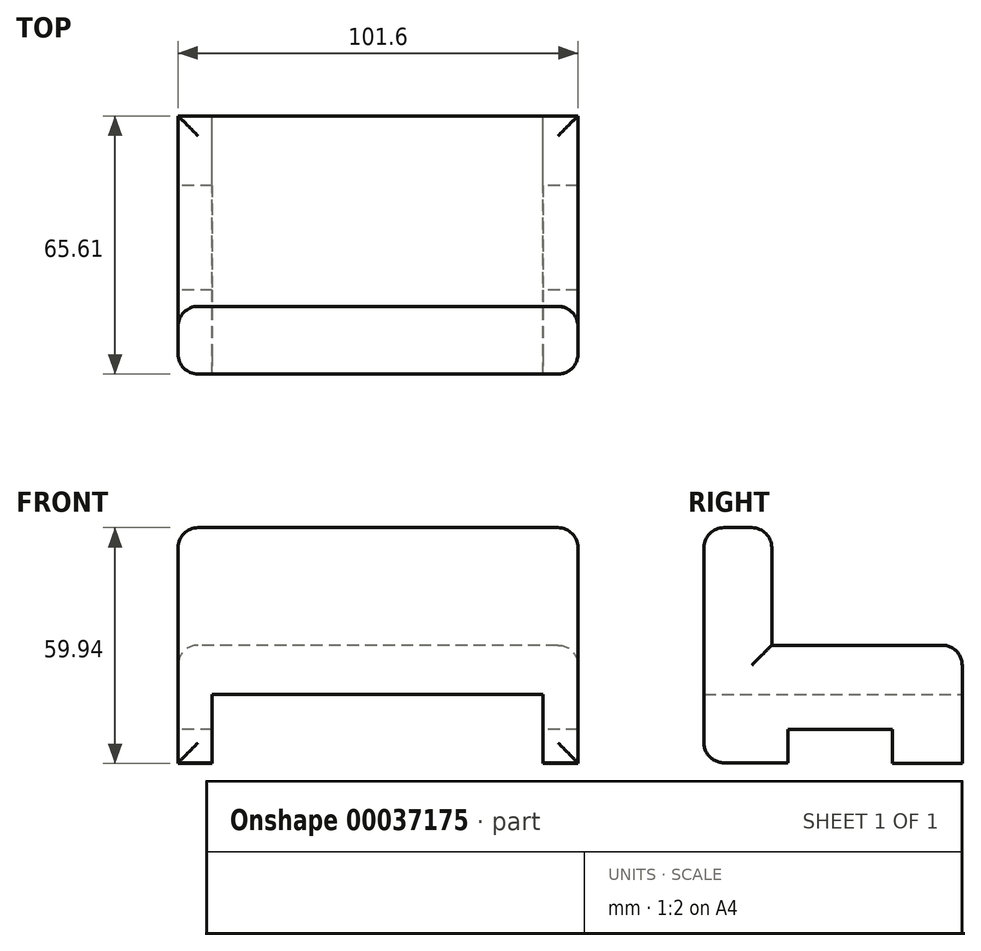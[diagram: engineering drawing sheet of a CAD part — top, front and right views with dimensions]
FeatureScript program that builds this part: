
annotation { "Feature Type Name" : "Feature", "Feature Type Description" : "" }
export const myFeature = defineFeature(function(context is Context, id is Id, definition is map)
    precondition{}
    {
        {
            var Q0;
            Q0=qCreatedBy(makeId("Right.planeOp"),FACE);
            var sketch = newSketch(context, id + "F0", { "sketchPlane" : qUnion([Q0])});
            skLineSegment(sketch, "E0", {"start": v(-63.82, 33.86) * mm, "end": v(-63.82, -25.87) * mm});
            skLineSegment(sketch, "E1", {"start": v(-63.82, -25.87) * mm, "end": v(-42.46, -25.87) * mm});
            skLineSegment(sketch, "E2", {"start": v(-42.46, -25.87) * mm, "end": v(-42.46, -17.37) * mm});
            skLineSegment(sketch, "E3", {"start": v(-42.46, -17.37) * mm, "end": v(-15.87, -17.37) * mm});
            skLineSegment(sketch, "E4", {"start": v(-15.87, -17.37) * mm, "end": v(-15.87, -26.08) * mm});
            skLineSegment(sketch, "E5", {"start": v(-15.87, -26.08) * mm, "end": v(1.8, -26.08) * mm});
            skLineSegment(sketch, "E6", {"start": v(1.8, -26.08) * mm, "end": v(1.8, 4) * mm});
            skLineSegment(sketch, "E7", {"start": v(1.8, 4) * mm, "end": v(-46.6, 4) * mm});
            skLineSegment(sketch, "E8", {"start": v(-46.6, 4) * mm, "end": v(-46.6, 33.86) * mm});
            skLineSegment(sketch, "E9", {"start": v(-46.6, 33.86) * mm, "end": v(-63.82, 33.86) * mm});
            skSolve(sketch);
        }
        {
            var Q0;
            Q0 = qSketchRegion(id + "F0", true);
            extrude(context, id + "F1", {"entities" : qUnion([Q0]), "depth" : 101.6 * mm});
        }
        {
            var Q0;
            Q0=makeQuery(id+"F1.opExtrude","SWEPT_FACE",FACE,{"disambiguationData":[OSD([sQuery(id+"F0.wireOp",EDGE,"E0")])]});
            var Q1;
            Q1=makeQuery(id+"F1.opExtrude","SWEPT_EDGE",EDGE,{"disambiguationData":[OSD([sQuery(id+"F0.wireOp",EDGE,"E6"),sQuery(id+"F0.wireOp",EDGE,"E7")])]});
            var Q2;
            Q2=makeQuery(id+"F1.opExtrude","CAP_EDGE",EDGE,{"disambiguationData":[OSD([sQuery(id+"F0.wireOp",EDGE,"E7")])],"isStart":false});
            var Q3;
            Q3=makeQuery(id+"F1.opExtrude","CAP_EDGE",EDGE,{"disambiguationData":[OSD([sQuery(id+"F0.wireOp",EDGE,"E7")])],"isStart":true});
            var Q4;
            Q4=makeQuery(id+"F1.opExtrude","CAP_EDGE",EDGE,{"disambiguationData":[OSD([sQuery(id+"F0.wireOp",EDGE,"E9")])],"isStart":true});
            var Q5;
            Q5=makeQuery(id+"F1.opExtrude","SWEPT_EDGE",EDGE,{"disambiguationData":[OSD([sQuery(id+"F0.wireOp",EDGE,"E8"),sQuery(id+"F0.wireOp",EDGE,"E9")])]});
            var Q6;
            Q6=makeQuery(id+"F1.opExtrude","CAP_EDGE",EDGE,{"disambiguationData":[OSD([sQuery(id+"F0.wireOp",EDGE,"E9")])],"isStart":false});
            var Q7;
            Q7=makeQuery(id+"F1.opExtrude","CAP_EDGE",EDGE,{"disambiguationData":[OSD([sQuery(id+"F0.wireOp",EDGE,"E8")])],"isStart":false});
            var Q8;
            Q8=makeQuery(id+"F1.opExtrude","CAP_EDGE",EDGE,{"disambiguationData":[OSD([sQuery(id+"F0.wireOp",EDGE,"E8")])],"isStart":true});
            fillet(context, id + "F2", {"entities" : qUnion([Q0, Q1, Q2, Q3, Q4, Q5, Q6, Q7, Q8]), "radius" : 5.08 * mm, "tangentPropagation" : true, "allowEdgeOverflow" : false});
        }
        {
            var Q0;
            Q0=makeQuery(id+"F1.opExtrude","SWEPT_FACE",FACE,{"disambiguationData":[OSD([sQuery(id+"F0.wireOp",EDGE,"E6")])]});
            var sketch = newSketch(context, id + "F3", { "sketchPlane" : qUnion([Q0])});
            skLineSegment(sketch, "E10.bottom", {"start": v(-92.74, -26.08) * mm, "end": v(-8.67, -26.08) * mm});
            skLineSegment(sketch, "E10.top", {"start": v(-92.74, -8.57) * mm, "end": v(-8.67, -8.57) * mm});
            skLineSegment(sketch, "E10.left", {"start": v(-92.74, -26.08) * mm, "end": v(-92.74, -8.57) * mm});
            skLineSegment(sketch, "E10.right", {"start": v(-8.67, -26.08) * mm, "end": v(-8.67, -8.57) * mm});
            skSolve(sketch);
        }
        {
            var Q0;
            Q0=makeQuery(id+"F3.imprint","IMPRINT",FACE,{"disambiguationData":[TD([[makeQuery(id+"F3.imprint","IMPRINT",EDGE,{"derivedFrom":sQuery(id+"F3.wireOp",EDGE,"E10.bottom")}),1.0]])]});
            extrude(context, id + "F4", {"entities" : qUnion([Q0]), "operationType" : NewBodyOperationType.REMOVE, "endBound" : BoundingType.THROUGH_ALL, "oppositeDirection" : true, "depth" : 25.4 * mm});
        }
    });
